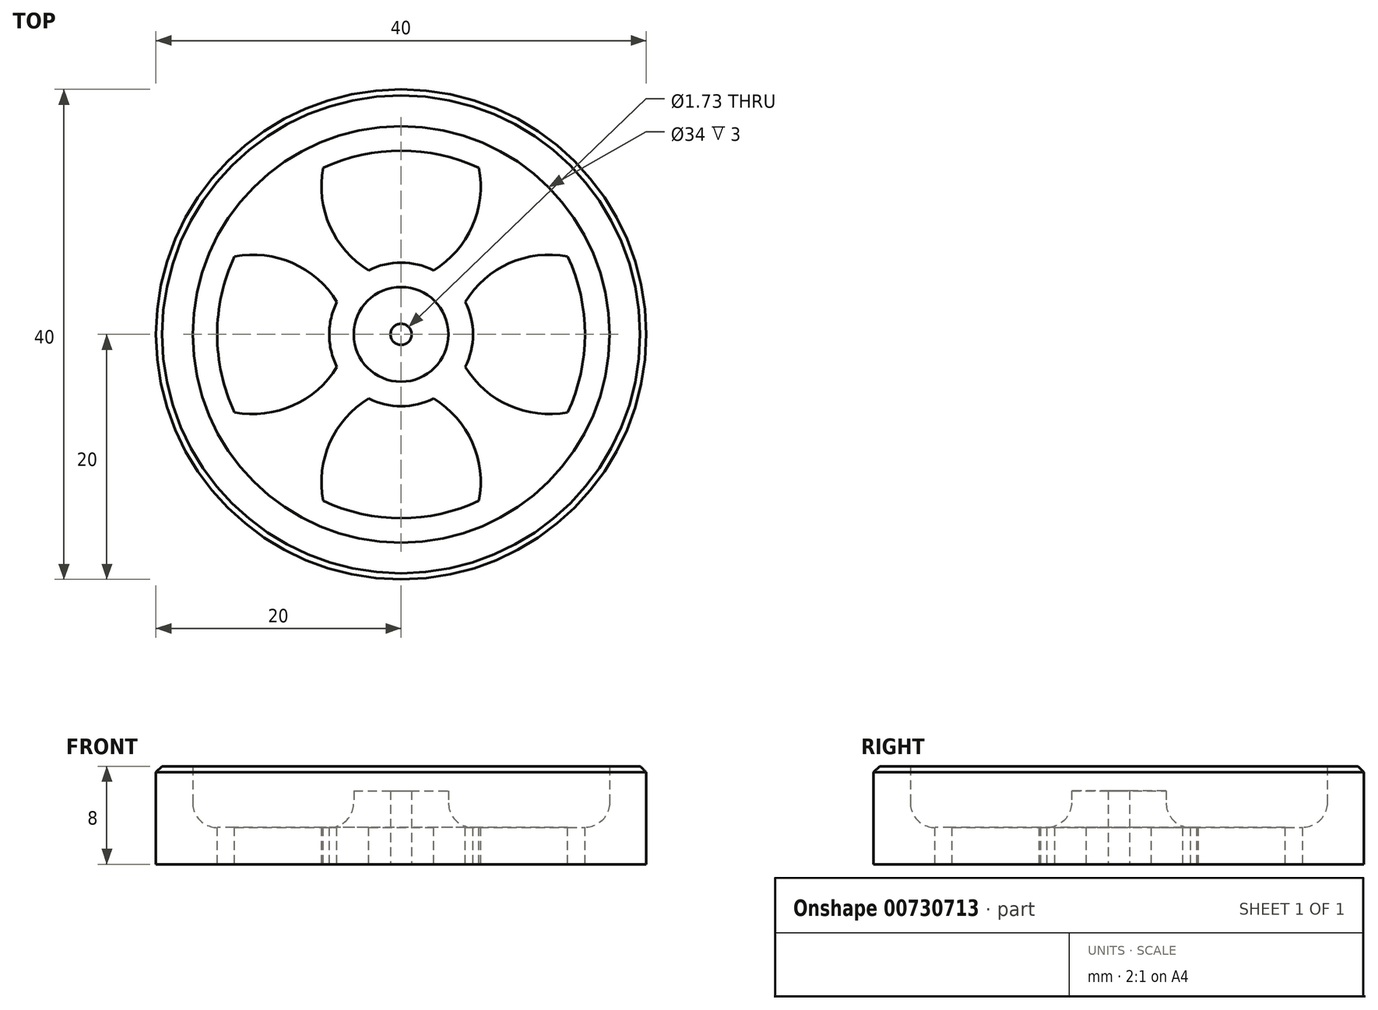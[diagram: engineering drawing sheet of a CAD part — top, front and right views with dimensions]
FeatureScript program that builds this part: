
annotation { "Feature Type Name" : "Feature", "Feature Type Description" : "" }
export const myFeature = defineFeature(function(context is Context, id is Id, definition is map)
    precondition{}
    {
        {
            var Q0;
            Q0=qCreatedBy(makeId("Front.planeOp"),FACE);
            var sketch = newSketch(context, id + "F0", { "sketchPlane" : qUnion([Q0])});
            skLineSegment(sketch, "E0", {"start": v(0, -3.5) * mm, "end": v(0, 21.94) * mm, "construction": true});
            skLineSegment(sketch, "E1", {"start": v(0.86, 0) * mm, "end": v(20, 0) * mm});
            skLineSegment(sketch, "E2", {"start": v(20, 0) * mm, "end": v(20, 8) * mm});
            skLineSegment(sketch, "E3", {"start": v(20, 8) * mm, "end": v(17, 8) * mm});
            skLineSegment(sketch, "E4", {"start": v(17, 8) * mm, "end": v(17, 5) * mm});
            skLineSegment(sketch, "E5", {"start": v(15, 3) * mm, "end": v(5.86, 3) * mm});
            skLineSegment(sketch, "E6", {"start": v(3.86, 5) * mm, "end": v(3.86, 6) * mm});
            skLineSegment(sketch, "E7", {"start": v(3.86, 6) * mm, "end": v(0.86, 6) * mm});
            skLineSegment(sketch, "E8", {"start": v(0.86, 6) * mm, "end": v(0.86, 0) * mm});
            skPoint(sketch, "E9.visualSharp", {"position": v(17, 3) * mm});
            skArc(sketch, "E9.filletArc", {"start": v(15, 3) * mm, "mid": v(16.41, 3.59) * mm, "end": v(17, 5) * mm});
            skPoint(sketch, "E10.visualSharp", {"position": v(3.86, 3) * mm});
            skArc(sketch, "E10.filletArc", {"start": v(3.86, 5) * mm, "mid": v(4.45, 3.59) * mm, "end": v(5.86, 3) * mm});
            skSolve(sketch);
        }
        {
            var Q0;
            Q0 = qSketchRegion(id + "F0", true);
            var Q1;
            Q1=sQuery(id+"F0.wireOp",EDGE,"E0");
            revolve(context, id + "F1", {"surfaceOperationType" : NewSurfaceOperationType.NEW, "entities" : qUnion([Q0]), "axis" : qUnion([Q1]), "revolveType" : RevolveType.FULL});
        }
        {
            var Q0;
            Q0=makeQuery(id+"F1.opRevolve","SWEPT_EDGE",EDGE,{"disambiguationData":[OSD([sQuery(id+"F0.wireOp",EDGE,"E2"),sQuery(id+"F0.wireOp",EDGE,"E3")])]});
            chamfer(context, id + "F2", {"entities" : qUnion([Q0]), "width" : .5 * mm, "tangentPropagation" : true});
        }
        {
            var Q0;
            Q0=makeQuery(id+"F1.opRevolve","SWEPT_FACE",FACE,{"disambiguationData":[OSD([sQuery(id+"F0.wireOp",EDGE,"E5")])]});
            var sketch = newSketch(context, id + "F3", { "sketchPlane" : qUnion([Q0])});
            skArc(sketch, "E11.0", {"start": v(5.23, 2.64) * mm, "mid": v(5.7, 1.36) * mm, "end": v(5.86, 0) * mm});
            skArc(sketch, "E12.0", {"start": v(13.59, 6.36) * mm, "mid": v(14.64, 3.26) * mm, "end": v(15, 0) * mm});
            skArc(sketch, "E13", {"start": v(13.59, 6.36) * mm, "mid": v(8.83, 5.81) * mm, "end": v(5.23, 2.64) * mm});
            skLineSegment(sketch, "E14", {"start": v(0, 0) * mm, "end": v(14.9, 14.9) * mm, "construction": true});
            skLineSegment(sketch, "E15", {"start": v(0, 0) * mm, "end": v(27.61, 0) * mm, "construction": true});
            skArc(sketch, "E16.MirrorCS", {"start": v(5.23, -2.64) * mm, "mid": v(5.7, -1.36) * mm, "end": v(5.86, 0) * mm});
            skArc(sketch, "E17.MirrorCS", {"start": v(13.59, -6.36) * mm, "mid": v(14.64, -3.26) * mm, "end": v(15, 0) * mm});
            skArc(sketch, "E18.MirrorCS", {"start": v(13.59, -6.36) * mm, "mid": v(8.83, -5.81) * mm, "end": v(5.23, -2.64) * mm});
            skArc(sketch, "E19.1.0", {"start": v(-6.36, 13.59) * mm, "mid": v(-5.81, 8.83) * mm, "end": v(-2.64, 5.23) * mm});
            skArc(sketch, "E19.1.1", {"start": v(2.64, 5.23) * mm, "mid": v(1.36, 5.7) * mm, "end": v(0, 5.86) * mm});
            skArc(sketch, "E19.1.2", {"start": v(-6.36, 13.59) * mm, "mid": v(-3.26, 14.64) * mm, "end": v(0, 15) * mm});
            skArc(sketch, "E19.1.3", {"start": v(-2.64, 5.23) * mm, "mid": v(-1.36, 5.7) * mm, "end": v(0, 5.86) * mm});
            skArc(sketch, "E19.1.4", {"start": v(6.36, 13.59) * mm, "mid": v(3.26, 14.64) * mm, "end": v(0, 15) * mm});
            skArc(sketch, "E19.1.5", {"start": v(6.36, 13.59) * mm, "mid": v(5.81, 8.83) * mm, "end": v(2.64, 5.23) * mm});
            skArc(sketch, "E19.2.0", {"start": v(-13.59, -6.36) * mm, "mid": v(-8.83, -5.81) * mm, "end": v(-5.23, -2.64) * mm});
            skArc(sketch, "E19.2.1", {"start": v(-5.23, 2.64) * mm, "mid": v(-5.7, 1.36) * mm, "end": v(-5.86, 0) * mm});
            skArc(sketch, "E19.2.2", {"start": v(-13.59, -6.36) * mm, "mid": v(-14.64, -3.26) * mm, "end": v(-15, 0) * mm});
            skArc(sketch, "E19.2.3", {"start": v(-5.23, -2.64) * mm, "mid": v(-5.7, -1.36) * mm, "end": v(-5.86, 0) * mm});
            skArc(sketch, "E19.2.4", {"start": v(-13.59, 6.36) * mm, "mid": v(-14.64, 3.26) * mm, "end": v(-15, 0) * mm});
            skArc(sketch, "E19.2.5", {"start": v(-13.59, 6.36) * mm, "mid": v(-8.83, 5.81) * mm, "end": v(-5.23, 2.64) * mm});
            skArc(sketch, "E19.3.0", {"start": v(6.36, -13.59) * mm, "mid": v(5.81, -8.83) * mm, "end": v(2.64, -5.23) * mm});
            skArc(sketch, "E19.3.1", {"start": v(-2.64, -5.23) * mm, "mid": v(-1.36, -5.7) * mm, "end": v(0, -5.86) * mm});
            skArc(sketch, "E19.3.2", {"start": v(6.36, -13.59) * mm, "mid": v(3.26, -14.64) * mm, "end": v(0, -15) * mm});
            skArc(sketch, "E19.3.3", {"start": v(2.64, -5.23) * mm, "mid": v(1.36, -5.7) * mm, "end": v(0, -5.86) * mm});
            skArc(sketch, "E19.3.4", {"start": v(-6.36, -13.59) * mm, "mid": v(-3.26, -14.64) * mm, "end": v(0, -15) * mm});
            skArc(sketch, "E19.3.5", {"start": v(-6.36, -13.59) * mm, "mid": v(-5.81, -8.83) * mm, "end": v(-2.64, -5.23) * mm});
            skSolve(sketch);
        }
        {
            var Q0;
            Q0 = qSketchRegion(id + "F3", true);
            var Q1;
            Q1=makeQuery(id+"F1.opRevolve","SWEPT_FACE",FACE,{"disambiguationData":[OSD([sQuery(id+"F0.wireOp",EDGE,"E1")])]});
            extrude(context, id + "F4", {"entities" : qUnion([Q0]), "operationType" : NewBodyOperationType.REMOVE, "endBound" : BoundingType.UP_TO_SURFACE, "oppositeDirection" : true, "depth" : 25 * mm, "endBoundEntityFace" : qUnion([Q1]), "offsetDistance" : 25 * mm});
        }
    });
